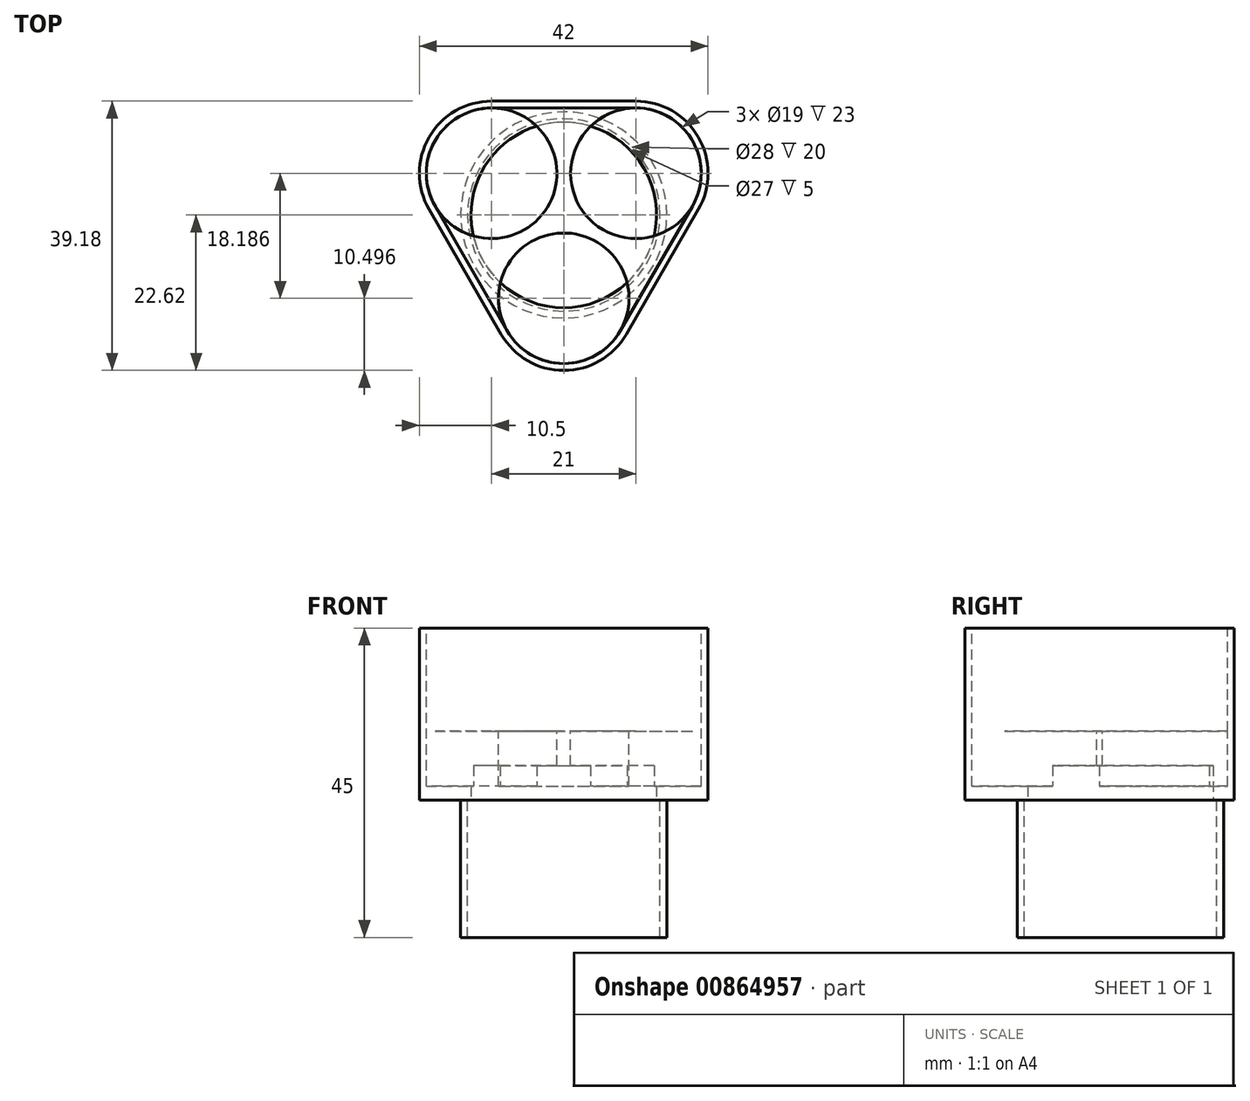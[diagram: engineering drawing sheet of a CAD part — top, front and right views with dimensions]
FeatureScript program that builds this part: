
annotation { "Feature Type Name" : "Feature", "Feature Type Description" : "" }
export const myFeature = defineFeature(function(context is Context, id is Id, definition is map)
    precondition{}
    {
        {
            var Q0;
            Q0=qCreatedBy(makeId("Top.planeOp"),FACE);
            var sketch = newSketch(context, id + "F0", { "sketchPlane" : qUnion([Q0])});
            skCircle(sketch, "E0", {"center": v(0, 0) * mm, "radius": 15 * mm});
            skSolve(sketch);
        }
        {
            var Q0;
            Q0 = qSketchRegion(id + "F0", true);
            extrude(context, id + "F1", {"entities" : qUnion([Q0]), "depth" : 20 * mm, "offsetDistance" : 25 * mm});
        }
        {
            var Q0;
            Q0=makeQuery(id+"F1.opExtrude","CAP_FACE",FACE,{"disambiguationData":[OSD([sQuery(id+"F0.wireOp",EDGE,"E0")])],"isStart":false});
            var sketch = newSketch(context, id + "F2", { "sketchPlane" : qUnion([Q0])});
            skCircle(sketch, "E1", {"center": v(0, 0) * mm, "radius": 14 * mm});
            skSolve(sketch);
        }
        {
            var Q0;
            Q0 = qSketchRegion(id + "F2", true);
            extrude(context, id + "F3", {"entities" : qUnion([Q0]), "operationType" : NewBodyOperationType.REMOVE, "oppositeDirection" : true, "depth" : 20 * mm, "offsetDistance" : 25 * mm});
        }
        {
            var Q0;
            Q0=makeQuery(id+"F1.opExtrude","CAP_FACE",FACE,{"disambiguationData":[OSD([sQuery(id+"F0.wireOp",EDGE,"E0")])],"isStart":false});
            var sketch = newSketch(context, id + "F4", { "sketchPlane" : qUnion([Q0])});
            skArc(sketch, "E2", {"start": v(-10.5, 16.56) * mm, "mid": v(-19.6, 11.31) * mm, "end": v(-19.6, 0.81) * mm});
            skArc(sketch, "E3", {"start": v(19.6, 0.81) * mm, "mid": v(19.6, 11.31) * mm, "end": v(10.5, 16.56) * mm});
            skArc(sketch, "E4", {"start": v(-9.1, -17.37) * mm, "mid": v(0, -22.62) * mm, "end": v(9.1, -17.37) * mm});
            skLineSegment(sketch, "E5", {"start": v(-19.6, 0.81) * mm, "end": v(-9.1, -17.37) * mm});
            skLineSegment(sketch, "E6", {"start": v(9.1, -17.37) * mm, "end": v(19.6, 0.81) * mm});
            skLineSegment(sketch, "E7", {"start": v(-10.5, 16.56) * mm, "end": v(10.5, 16.56) * mm});
            skSolve(sketch);
        }
        {
            var Q0;
            Q0 = qSketchRegion(id + "F4", true);
            extrude(context, id + "F5", {"entities" : qUnion([Q0]), "operationType" : NewBodyOperationType.ADD, "depth" : 25 * mm, "offsetDistance" : 25 * mm});
        }
        {
            var Q0;
            Q0=makeQuery(id+"F5.opExtrude","CAP_FACE",FACE,{"disambiguationData":[OSD([sQuery(id+"F4.wireOp",EDGE,"E2"),sQuery(id+"F4.wireOp",EDGE,"E3"),sQuery(id+"F4.wireOp",EDGE,"E4"),sQuery(id+"F4.wireOp",EDGE,"E5"),sQuery(id+"F4.wireOp",EDGE,"E6"),sQuery(id+"F4.wireOp",EDGE,"E7")])],"isStart":false});
            var sketch = newSketch(context, id + "F6", { "sketchPlane" : qUnion([Q0])});
            skCircle(sketch, "E8", {"center": v(10.5, 6.06) * mm, "radius": 9.5 * mm});
            skCircle(sketch, "E9", {"center": v(0, -12.12) * mm, "radius": 9.5 * mm});
            skCircle(sketch, "E10", {"center": v(-10.5, 6.06) * mm, "radius": 9.5 * mm});
            skSolve(sketch);
        }
        {
            var Q0;
            Q0 = qSketchRegion(id + "F6", true);
            extrude(context, id + "F7", {"entities" : qUnion([Q0]), "operationType" : NewBodyOperationType.REMOVE, "oppositeDirection" : true, "depth" : 23 * mm, "offsetDistance" : 25 * mm});
        }
        {
            var Q0;
            Q0=makeQuery(id+"F5.opExtrude","CAP_FACE",FACE,{"disambiguationData":[OSD([sQuery(id+"F4.wireOp",EDGE,"E2"),sQuery(id+"F4.wireOp",EDGE,"E3"),sQuery(id+"F4.wireOp",EDGE,"E4"),sQuery(id+"F4.wireOp",EDGE,"E5"),sQuery(id+"F4.wireOp",EDGE,"E6"),sQuery(id+"F4.wireOp",EDGE,"E7")])],"isStart":false});
            var sketch = newSketch(context, id + "F8", { "sketchPlane" : qUnion([Q0])});
            skCircle(sketch, "E11", {"center": v(10.5, 6.06) * mm, "radius": 9.5 * mm});
            skCircle(sketch, "E12", {"center": v(-10.5, 6.06) * mm, "radius": 9.5 * mm});
            skCircle(sketch, "E13", {"center": v(0, -12.12) * mm, "radius": 9.5 * mm});
            skLineSegment(sketch, "E14", {"start": v(-10.5, 15.56) * mm, "end": v(10.5, 15.56) * mm});
            skLineSegment(sketch, "E15", {"start": v(-8.23, -16.87) * mm, "end": v(-18.73, 1.31) * mm});
            skLineSegment(sketch, "E16", {"start": v(8.23, -16.87) * mm, "end": v(18.73, 1.31) * mm});
            skSolve(sketch);
        }
        {
            var Q0;
            Q0 = qSketchRegion(id + "F8", true);
            extrude(context, id + "F9", {"entities" : qUnion([Q0]), "operationType" : NewBodyOperationType.REMOVE, "oppositeDirection" : true, "depth" : 15 * mm, "offsetDistance" : 25 * mm});
        }
        {
            var Q0;
            Q0=makeQuery(id+"F5.boolean.opBoolean","SPLIT",FACE,{"disambiguationData":[TD([makeQuery(id+"F3.boolean.opBoolean","COPY",FACE,{"derivedFrom":makeQuery(id+"F3.opExtrude","SWEPT_FACE",FACE,{"disambiguationData":[OSD([sQuery(id+"F2.wireOp",EDGE,"E1")])]})})])],"derivedFrom":makeQuery(id+"F5.opExtrude","CAP_FACE",FACE,{"disambiguationData":[OSD([sQuery(id+"F4.wireOp",EDGE,"E2"),sQuery(id+"F4.wireOp",EDGE,"E3"),sQuery(id+"F4.wireOp",EDGE,"E4"),sQuery(id+"F4.wireOp",EDGE,"E5"),sQuery(id+"F4.wireOp",EDGE,"E6"),sQuery(id+"F4.wireOp",EDGE,"E7")])],"isStart":true})});
            var sketch = newSketch(context, id + "F10", { "sketchPlane" : qUnion([Q0])});
            skCircle(sketch, "E17", {"center": v(0, 0) * mm, "radius": 13.5 * mm});
            skSolve(sketch);
        }
        {
            var Q0;
            Q0 = qSketchRegion(id + "F10", true);
            extrude(context, id + "F11", {"entities" : qUnion([Q0]), "operationType" : NewBodyOperationType.REMOVE, "oppositeDirection" : true, "depth" : 5 * mm, "offsetDistance" : 25 * mm});
        }
    });
